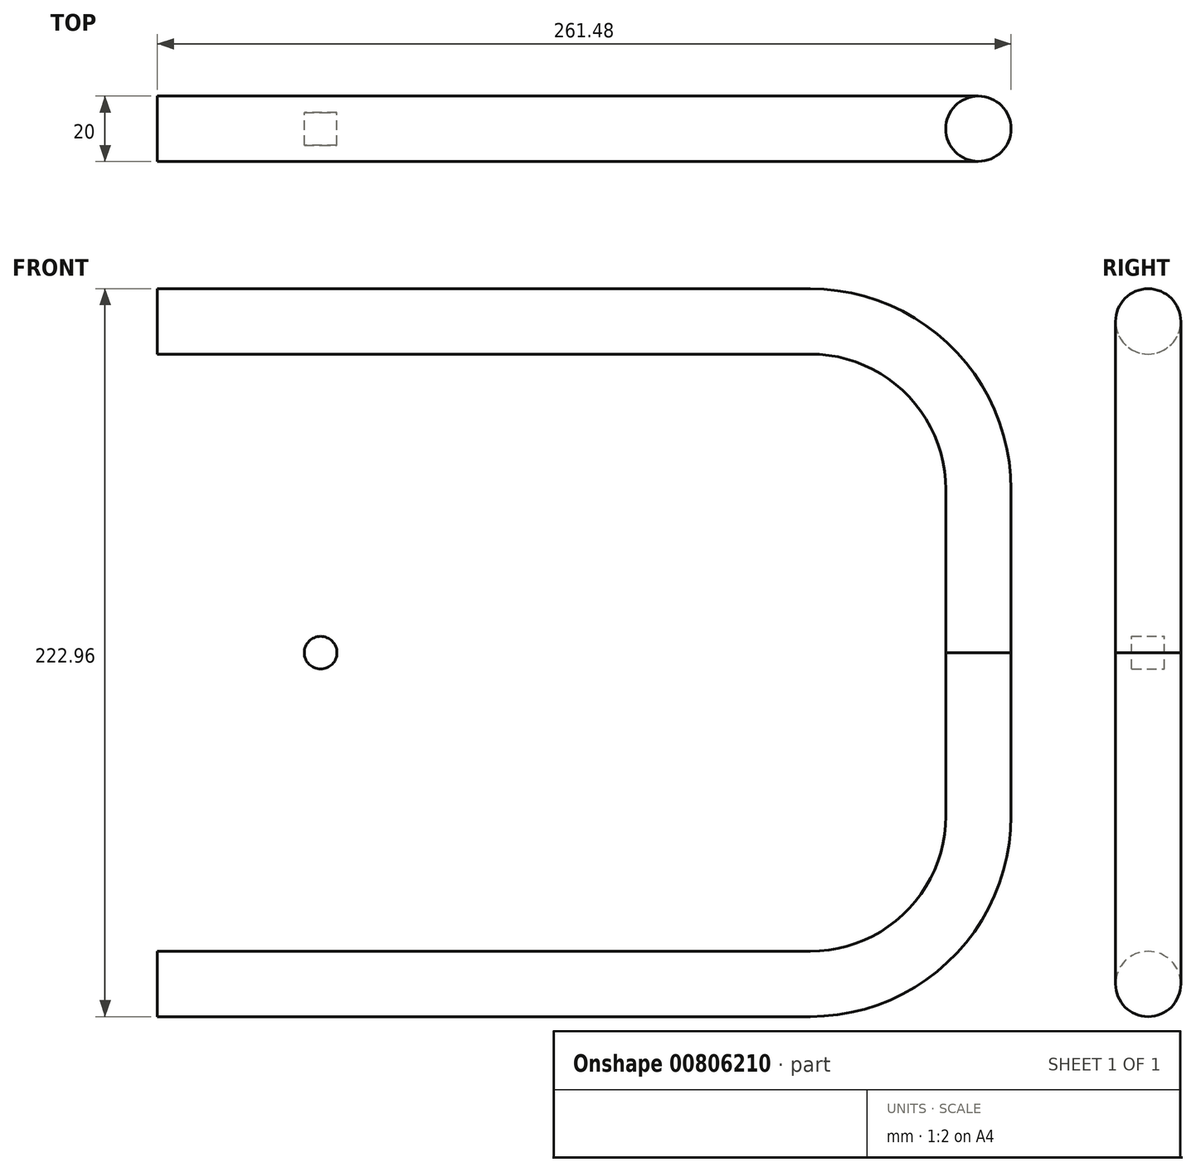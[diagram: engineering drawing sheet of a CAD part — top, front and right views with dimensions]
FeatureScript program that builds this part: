
annotation { "Feature Type Name" : "Feature", "Feature Type Description" : "" }
export const myFeature = defineFeature(function(context is Context, id is Id, definition is map)
    precondition{}
    {
        {
            var Q0;
            Q0=qCreatedBy(makeId("Front.planeOp"),FACE);
            var sketch = newSketch(context, id + "F0", { "sketchPlane" : qUnion([Q0])});
            skLineSegment(sketch, "E0.bottom", {"start": v(0, 0) * mm, "end": v(200, 0) * mm});
            skLineSegment(sketch, "E0.top", {"start": v(0, -100) * mm, "end": v(150, -100) * mm});
            skLineSegment(sketch, "E0.left", {"start": v(0, 0) * mm, "end": v(0, -100) * mm});
            skLineSegment(sketch, "E0.right", {"start": v(200, 0) * mm, "end": v(200, -50) * mm});
            skCircle(sketch, "E1", {"center": v(0, 0) * mm, "radius": 5 * mm});
            skPoint(sketch, "E2.visualSharp", {"position": v(200, -100) * mm});
            skArc(sketch, "E2.filletArc", {"start": v(150, -100) * mm, "mid": v(185.36, -85.36) * mm, "end": v(200, -50) * mm});
            skLineSegment(sketch, "E3", {"start": v(0, -100) * mm, "end": v(-50, -100) * mm});
            skSolve(sketch);
        }
        {
            var Q0;
            {var subQ0=sQuery(id+"F0.wireOp",EDGE,"E0.left");var subQ1=sQuery(id+"F0.wireOp",EDGE,"E0.bottom");var subQ2=makeQuery(id+"F0.imprint","INTERSECT",VERTEX,{"derivedFrom":[subQ1,subQ0]});Q0=makeQuery(id+"F0.imprint","IMPRINT",FACE,{"disambiguationData":[TD([[makeQuery(id+"F0.imprint","IMPRINT",EDGE,{"disambiguationData":[TD([[subQ2,-1.0]])],"derivedFrom":subQ1}),1.0]])]});}
            var Q1;
            {var subQ0=sQuery(id+"F0.wireOp",EDGE,"E0.left");var subQ1=sQuery(id+"F0.wireOp",EDGE,"E0.bottom");var subQ2=makeQuery(id+"F0.imprint","INTERSECT",VERTEX,{"derivedFrom":[subQ1,subQ0]});Q1=makeQuery(id+"F0.imprint","IMPRINT",FACE,{"disambiguationData":[TD([[makeQuery(id+"F0.imprint","IMPRINT",EDGE,{"disambiguationData":[TD([[subQ2,-1.0]])],"derivedFrom":subQ1}),-1.0]])]});}
            extrude(context, id + "F1", {"entities" : qUnion([Q0, Q1]), "endBound" : BoundingType.SYMMETRIC, "depth" : 10 * mm, "offsetDistance" : 25 * mm});
        }
        {
            var Q0;
            Q0=qCreatedBy(makeId("Top.planeOp"),FACE);
            var sketch = newSketch(context, id + "F2", { "sketchPlane" : qUnion([Q0])});
            skCircle(sketch, "E4", {"center": v(201.48, 0) * mm, "radius": 10 * mm});
            skSolve(sketch);
        }
        {
            var Q0;
            Q0=makeQuery(id+"F2.imprint","IMPRINT",FACE,{"disambiguationData":[TD([[makeQuery(id+"F2.imprint","IMPRINT",EDGE,{"derivedFrom":sQuery(id+"F2.wireOp",EDGE,"E4")}),1.0]])]});
            var Q1;
            Q1=sQuery(id+"F0.wireOp",EDGE,"E0.right");
            var Q2;
            Q2=sQuery(id+"F0.wireOp",EDGE,"E2.filletArc");
            var Q3;
            Q3=sQuery(id+"F0.wireOp",EDGE,"E0.top");
            var Q4;
            Q4=sQuery(id+"F0.wireOp",EDGE,"E3");
            sweep(context, id + "F3", {"profiles" : qUnion([Q0]), "path" : qUnion([Q1, Q2, Q3, Q4])});
        }
        {
            var Q0;
            Q0=makeQuery(id+"F3.opSweep","SWEPT_BODY",BODY,{"disambiguationData":[OSD([sQuery(id+"F0.wireOp",EDGE,"E0.top"),sQuery(id+"F2.wireOp",EDGE,"E4")])]});
            var Q1;
            Q1=makeQuery(id+"F3.opSweep","CAP_FACE",FACE,{"disambiguationData":[OSD([sQuery(id+"F0.wireOp",VERTEX,"E0.right.start"),sQuery(id+"F2.wireOp",EDGE,"E4")])],"isStart":true});
            mirror(context, id + "F4", {"operationType" : NewBodyOperationType.ADD, "entities" : qUnion([Q0]), "mirrorPlane" : qUnion([Q1])});
        }
    });
